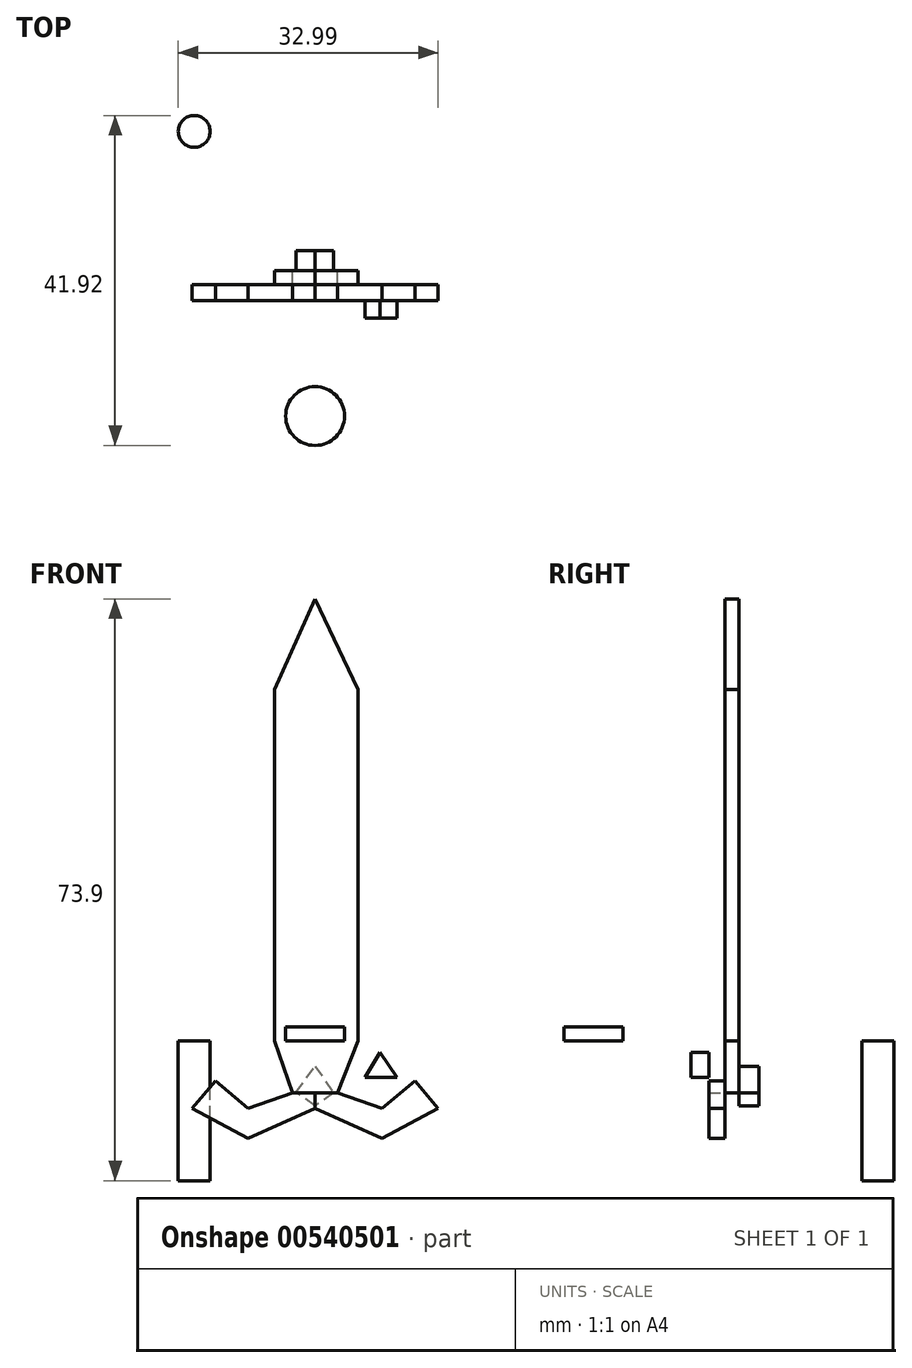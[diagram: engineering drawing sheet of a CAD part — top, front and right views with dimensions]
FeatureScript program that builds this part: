
annotation { "Feature Type Name" : "Feature", "Feature Type Description" : "" }
export const myFeature = defineFeature(function(context is Context, id is Id, definition is map)
    precondition{}
    {
        {
            var Q0;
            Q0=qCreatedBy(makeId("Front.planeOp"),FACE);
            var sketch = newSketch(context, id + "F0", { "sketchPlane" : qUnion([Q0])});
            skLineSegment(sketch, "E0", {"start": v(0, 56.12) * mm, "end": v(-5.18, 44.6) * mm});
            skLineSegment(sketch, "E1", {"start": v(-5.18, 44.6) * mm, "end": v(5.47, 44.6) * mm});
            skLineSegment(sketch, "E2", {"start": v(5.47, 44.6) * mm, "end": v(0, 56.12) * mm});
            skLineSegment(sketch, "E3.top", {"start": v(-5.18, 0) * mm, "end": v(5.47, 0) * mm});
            skLineSegment(sketch, "E3.left", {"start": v(-5.18, 44.6) * mm, "end": v(-5.18, 0) * mm});
            skLineSegment(sketch, "E3.right", {"start": v(5.47, 44.6) * mm, "end": v(5.47, 0) * mm});
            skLineSegment(sketch, "E4", {"start": v(-5.18, 0) * mm, "end": v(-2.88, -6.62) * mm});
            skLineSegment(sketch, "E5", {"start": v(-2.88, -6.62) * mm, "end": v(2.88, -6.62) * mm});
            skLineSegment(sketch, "E6", {"start": v(2.88, -6.62) * mm, "end": v(5.47, 0) * mm});
            skSolve(sketch);
        }
        {
            var Q0;
            Q0 = qSketchRegion(id + "F0", true);
            extrude(context, id + "F1", {"entities" : qUnion([Q0]), "depth" : 1.78 * mm, "offsetDistance" : 25.4 * mm});
        }
        {
            var Q0;
            Q0=makeQuery(id+"F1.opExtrude","CAP_FACE",FACE,{"disambiguationData":[OSD([sQuery(id+"F0.wireOp",EDGE,"E0"),sQuery(id+"F0.wireOp",EDGE,"E2"),sQuery(id+"F0.wireOp",EDGE,"E3.left"),sQuery(id+"F0.wireOp",EDGE,"E3.right"),sQuery(id+"F0.wireOp",EDGE,"E4"),sQuery(id+"F0.wireOp",EDGE,"E5"),sQuery(id+"F0.wireOp",EDGE,"E6")])],"isStart":false});
            var sketch = newSketch(context, id + "F2", { "sketchPlane" : qUnion([Q0])});
            skLineSegment(sketch, "E7", {"start": v(-2.88, -6.62) * mm, "end": v(-8.5, -8.58) * mm});
            skLineSegment(sketch, "E8", {"start": v(-8.5, -8.58) * mm, "end": v(-12.67, -5.08) * mm});
            skLineSegment(sketch, "E9", {"start": v(-12.67, -5.08) * mm, "end": v(-15.6, -8.58) * mm});
            skLineSegment(sketch, "E10", {"start": v(-15.6, -8.58) * mm, "end": v(-8.5, -12.38) * mm});
            skLineSegment(sketch, "E11", {"start": v(-8.5, -12.38) * mm, "end": v(0, -8.58) * mm});
            skLineSegment(sketch, "E12", {"start": v(0, -8.58) * mm, "end": v(0, -6.62) * mm});
            skLineSegment(sketch, "E13", {"start": v(0, -6.62) * mm, "end": v(-2.88, -6.62) * mm});
            skSolve(sketch);
        }
        {
            var Q0;
            Q0=makeQuery(id+"F2.imprint","IMPRINT",FACE,{"disambiguationData":[TD([[makeQuery(id+"F2.imprint","IMPRINT",EDGE,{"derivedFrom":sQuery(id+"F2.wireOp",EDGE,"E7")}),1.0]])]});
            extrude(context, id + "F3", {"entities" : qUnion([Q0]), "depth" : 2.03 * mm, "offsetDistance" : 25.4 * mm});
        }
        {
            var Q0;
            Q0=makeQuery(id+"F3.opExtrude","SWEPT_BODY",BODY,{"disambiguationData":[OSD([sQuery(id+"F2.wireOp",EDGE,"E7"),sQuery(id+"F2.wireOp",EDGE,"E8"),sQuery(id+"F2.wireOp",EDGE,"E9"),sQuery(id+"F2.wireOp",EDGE,"E10"),sQuery(id+"F2.wireOp",EDGE,"E11"),sQuery(id+"F2.wireOp",EDGE,"E12"),sQuery(id+"F2.wireOp",EDGE,"E13")])]});
            var Q1;
            Q1=qCreatedBy(makeId("Right.planeOp"),FACE);
            mirror(context, id + "F4", {"operationType" : NewBodyOperationType.ADD, "entities" : qUnion([Q0]), "mirrorPlane" : qUnion([Q1])});
        }
        {
            var Q0;
            Q0=qCreatedBy(makeId("Top.planeOp"),FACE);
            var sketch = newSketch(context, id + "F5", { "sketchPlane" : qUnion([Q0])});
            skCircle(sketch, "E14", {"center": v(-15.36, 17.69) * mm, "radius": 2.02 * mm});
            skSolve(sketch);
        }
        {
            var Q0;
            Q0 = qSketchRegion(id + "F5", true);
            extrude(context, id + "F6", {"entities" : qUnion([Q0]), "oppositeDirection" : true, "depth" : 17.78 * mm, "offsetDistance" : 25.4 * mm});
        }
        {
            var Q0;
            Q0=qCreatedBy(makeId("Front.planeOp"),FACE);
            var sketch = newSketch(context, id + "F7", { "sketchPlane" : qUnion([Q0])});
            skLineSegment(sketch, "E15", {"start": v(-2.42, -6.58) * mm, "end": v(0, -3.25) * mm});
            skLineSegment(sketch, "E16", {"start": v(0, -3.25) * mm, "end": v(2.34, -6.66) * mm});
            skLineSegment(sketch, "E17", {"start": v(2.34, -6.66) * mm, "end": v(0, -8.27) * mm});
            skLineSegment(sketch, "E18", {"start": v(0, -8.27) * mm, "end": v(-2.42, -6.58) * mm});
            skSolve(sketch);
        }
        {
            var Q0;
            Q0=makeQuery(id+"F7.imprint","IMPRINT",FACE,{"disambiguationData":[TD([[makeQuery(id+"F7.imprint","IMPRINT",EDGE,{"derivedFrom":sQuery(id+"F7.wireOp",EDGE,"E15")}),-1.0]])]});
            extrude(context, id + "F8", {"entities" : qUnion([Q0]), "depth" : 2.54 * mm, "offsetDistance" : 25.4 * mm});
        }
        {
            var Q0;
            Q0=makeQuery(id+"F8.opExtrude","CAP_FACE",FACE,{"disambiguationData":[OSD([sQuery(id+"F7.wireOp",EDGE,"E15"),sQuery(id+"F7.wireOp",EDGE,"E16"),sQuery(id+"F7.wireOp",EDGE,"E17"),sQuery(id+"F7.wireOp",EDGE,"E18")])],"isStart":true});
            extrude(context, id + "F9", {"entities" : qUnion([Q0]), "depth" : 2.54 * mm, "offsetDistance" : 25.4 * mm});
        }
        {
            var Q0;
            Q0=makeQuery(id+"F8.opExtrude","SWEPT_BODY",BODY,{"disambiguationData":[OSD([sQuery(id+"F7.wireOp",EDGE,"E15"),sQuery(id+"F7.wireOp",EDGE,"E16"),sQuery(id+"F7.wireOp",EDGE,"E17"),sQuery(id+"F7.wireOp",EDGE,"E18")])]});
            deleteBodies(context, id + "F10", {"entities" : qUnion([Q0])});
        }
        {
            var Q0;
            Q0=qCreatedBy(makeId("Top.planeOp"),FACE);
            var sketch = newSketch(context, id + "F11", { "sketchPlane" : qUnion([Q0])});
            skCircle(sketch, "E19", {"center": v(0, -18.48) * mm, "radius": 3.73 * mm});
            skSolve(sketch);
        }
        {
            var Q0;
            Q0 = qSketchRegion(id + "F11", true);
            extrude(context, id + "F12", {"entities" : qUnion([Q0]), "depth" : 1.78 * mm, "offsetDistance" : 25.4 * mm});
        }
        {
            var Q0;
            {var subQ0=makeQuery(id+"F3.opExtrude","CAP_FACE",FACE,{"disambiguationData":[OSD([sQuery(id+"F2.wireOp",EDGE,"E7"),sQuery(id+"F2.wireOp",EDGE,"E8"),sQuery(id+"F2.wireOp",EDGE,"E9"),sQuery(id+"F2.wireOp",EDGE,"E10"),sQuery(id+"F2.wireOp",EDGE,"E11"),sQuery(id+"F2.wireOp",EDGE,"E12"),sQuery(id+"F2.wireOp",EDGE,"E13")])],"isStart":false});Q0=makeQuery(id+"F4.boolean.opBoolean","MERGE",FACE,{"derivedFrom":[subQ0,makeQuery(id+"F4.opPattern","COPY",FACE,{"derivedFrom":subQ0,"instanceName":"1"})]});}
            var sketch = newSketch(context, id + "F13", { "sketchPlane" : qUnion([Q0])});
            skLineSegment(sketch, "E20", {"start": v(8.23, -1.5) * mm, "end": v(6.34, -4.67) * mm});
            skLineSegment(sketch, "E21", {"start": v(6.34, -4.67) * mm, "end": v(10.42, -4.67) * mm});
            skLineSegment(sketch, "E22", {"start": v(10.42, -4.67) * mm, "end": v(8.23, -1.5) * mm});
            skSolve(sketch);
        }
        {
            var Q0;
            Q0=makeQuery(id+"F13.imprint","IMPRINT",FACE,{"disambiguationData":[TD([[makeQuery(id+"F13.imprint","IMPRINT",EDGE,{"derivedFrom":sQuery(id+"F13.wireOp",EDGE,"E20")}),1.0]])]});
            var Q1;
            Q1 = qSketchRegion(id + "F13", true);
            extrude(context, id + "F14", {"entities" : qUnion([Q0, Q1]), "depth" : 1.72 * mm, "offsetDistance" : 25.4 * mm});
        }
        {
            var Q0;
            Q0=makeQuery(id+"F14.opExtrude","CAP_FACE",FACE,{"disambiguationData":[OSD([sQuery(id+"F13.wireOp",EDGE,"E20"),sQuery(id+"F13.wireOp",EDGE,"E21"),sQuery(id+"F13.wireOp",EDGE,"E22")])],"isStart":false});
            extrude(context, id + "F15", {"entities" : qUnion([Q0]), "operationType" : NewBodyOperationType.ADD, "depth" : 0.53 * mm, "offsetDistance" : 25.4 * mm});
        }
    });
